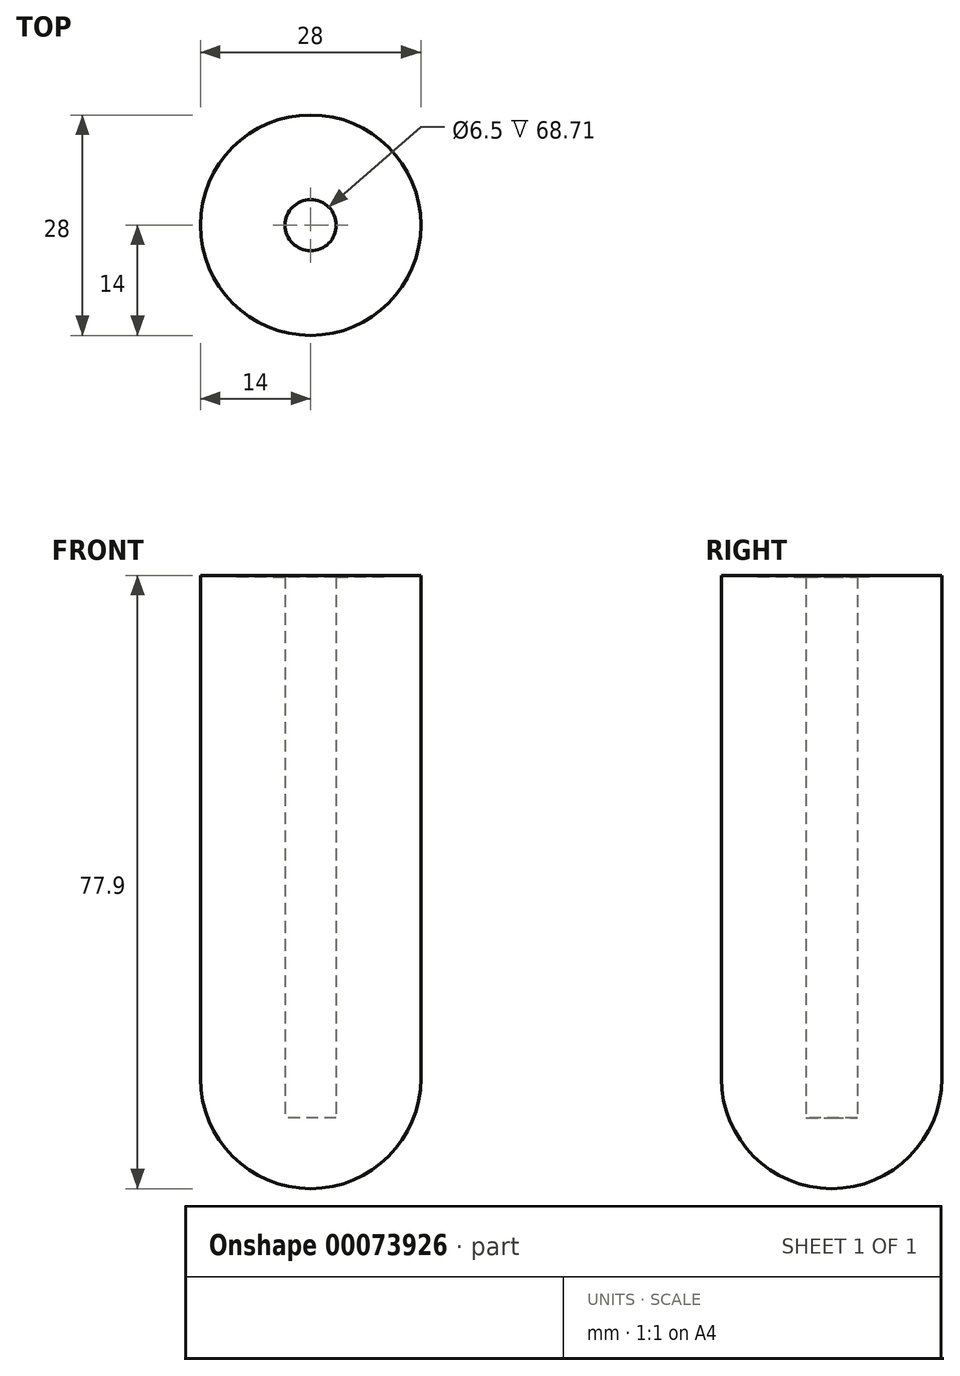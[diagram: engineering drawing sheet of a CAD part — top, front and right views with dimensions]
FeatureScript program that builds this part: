
annotation { "Feature Type Name" : "Feature", "Feature Type Description" : "" }
export const myFeature = defineFeature(function(context is Context, id is Id, definition is map)
    precondition{}
    {
        {
            var Q0;
            Q0=qCreatedBy(makeId("Top.planeOp"),FACE);
            var sketch = newSketch(context, id + "F0", { "sketchPlane" : qUnion([Q0])});
            skCircle(sketch, "E0", {"center": v(0, 0) * mm, "radius": 14 * mm});
            skSolve(sketch);
        }
        {
            var Q0;
            Q0 = qSketchRegion(id + "F0", true);
            extrude(context, id + "F1", {"entities" : qUnion([Q0]), "depth" : 64 * mm});
        }
        {
            var Q0;
            Q0=qCreatedBy(makeId("Front.planeOp"),FACE);
            var sketch = newSketch(context, id + "F2", { "sketchPlane" : qUnion([Q0])});
            skArc(sketch, "E1", {"start": v(-14, 0) * mm, "mid": v(0, -14) * mm, "end": v(14, 0) * mm});
            skLineSegment(sketch, "E2", {"start": v(-14, 0) * mm, "end": v(14, 0) * mm});
            skLineSegment(sketch, "E3", {"start": v(0, 0) * mm, "end": v(0, 8.37) * mm});
            skSolve(sketch);
        }
        {
            var Q0;
            {var subQ0=sQuery(id+"F2.wireOp",EDGE,"E1");Q0=makeQuery(id+"F2.imprint","IMPRINT",FACE,{"disambiguationData":[TD([[makeQuery(id+"F2.imprint","IMPRINT",EDGE,{"derivedFrom":subQ0}),1.0]])]});}
            var Q1;
            Q1=sQuery(id+"F2.wireOp",EDGE,"E2");
            revolve(context, id + "F3", {"operationType" : NewBodyOperationType.ADD, "entities" : qUnion([Q0]), "axis" : qUnion([Q1]), "revolveType" : RevolveType.FULL});
        }
        {
            var Q0;
            Q0=qCreatedBy(makeId("Front.planeOp"),FACE);
            var sketch = newSketch(context, id + "F4", { "sketchPlane" : qUnion([Q0])});
            skLineSegment(sketch, "E4", {"start": v(0, 0) * mm, "end": v(0, 64) * mm});
            skLineSegment(sketch, "E5", {"start": v(0, 64) * mm, "end": v(0, 67.7) * mm});
            skLineSegment(sketch, "E6", {"start": v(0, 67.7) * mm, "end": v(0, 71.7) * mm});
            skLineSegment(sketch, "E7", {"start": v(0, 67.7) * mm, "end": v(45, 67.7) * mm});
            skEllipticalArc(sketch, "E8", {});
            const initialGuessF4  = {"E8": [0, 0.0677, 1, 0, 0.045, 0.004, 4.71238898038469, 1.5707963267948966]};
            skSetInitialGuess(sketch, initialGuessF4);
            skSolve(sketch);
        }
        {
            var Q0;
            Q0=qCreatedBy(makeId("Top.planeOp"),FACE);
            cPlane(context, id + "F5", {"entities" : qUnion([Q0]), "cplaneType" : CPlaneType.OFFSET, "offset" : 5 * mm, "oppositeDirection" : true, "width" : 150 * mm, "height" : 150 * mm});
        }
        {
            var Q0;
            Q0=qCreatedBy(id+"F5.planeOp",FACE);
            var sketch = newSketch(context, id + "F6", { "sketchPlane" : qUnion([Q0])});
            skCircle(sketch, "E9", {"center": v(0, 0) * mm, "radius": 3.25 * mm});
            skSolve(sketch);
        }
        {
            var Q0;
            Q0 = qSketchRegion(id + "F6", true);
            extrude(context, id + "F7", {"entities" : qUnion([Q0]), "operationType" : NewBodyOperationType.REMOVE, "depth" : 69.14 * mm});
        }
        {
            var Q0;
            {var subQ0=sQuery(id+"F4.wireOp",EDGE,"E5");Q0=makeQuery(id+"F4.imprint","IMPRINT",FACE,{"disambiguationData":[TD([[makeQuery(id+"F4.imprint","IMPRINT",EDGE,{"derivedFrom":subQ0}),-1.0]])]});}
            var Q1;
            Q1=sQuery(id+"F4.wireOp",EDGE,"E5");
            revolve(context, id + "F8", {"operationType" : NewBodyOperationType.REMOVE, "entities" : qUnion([Q0]), "axis" : qUnion([Q1]), "revolveType" : RevolveType.FULL, "oppositeDirection" : true});
        }
    });
